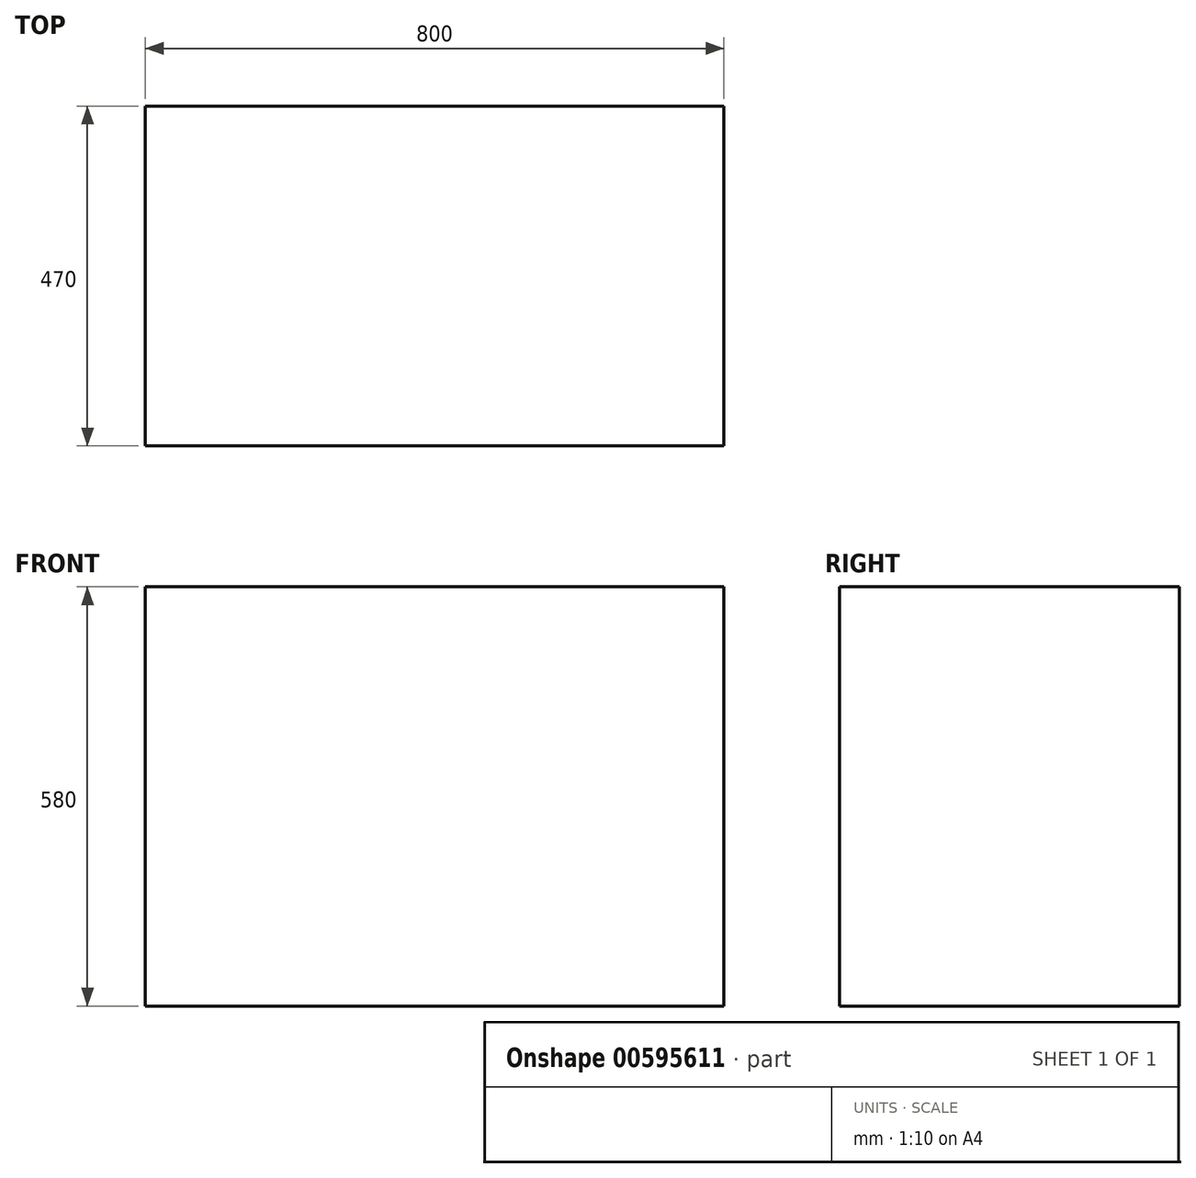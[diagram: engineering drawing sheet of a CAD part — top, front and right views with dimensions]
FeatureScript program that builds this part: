
annotation { "Feature Type Name" : "Feature", "Feature Type Description" : "" }
export const myFeature = defineFeature(function(context is Context, id is Id, definition is map)
    precondition{}
    {
        {
            var Q0;
            Q0=qCreatedBy(makeId("Front.planeOp"),FACE);
            var sketch = newSketch(context, id + "F0", { "sketchPlane" : qUnion([Q0])});
            skLineSegment(sketch, "E0.bottom", {"start": v(0, 0) * mm, "end": v(800, 0) * mm});
            skLineSegment(sketch, "E0.top", {"start": v(0, 580) * mm, "end": v(800, 580) * mm});
            skLineSegment(sketch, "E0.left", {"start": v(0, 0) * mm, "end": v(0, 580) * mm});
            skLineSegment(sketch, "E0.right", {"start": v(800, 0) * mm, "end": v(800, 580) * mm});
            skSolve(sketch);
        }
        {
            var Q0;
            Q0=makeQuery(id+"F0.imprint","IMPRINT",FACE,{"disambiguationData":[TD([[makeQuery(id+"F0.imprint","IMPRINT",EDGE,{"derivedFrom":sQuery(id+"F0.wireOp",EDGE,"E0.bottom")}),1.0]])]});
            extrude(context, id + "F1", {"entities" : qUnion([Q0]), "depth" : 470 * mm, "offsetDistance" : 25 * mm});
        }
    });
